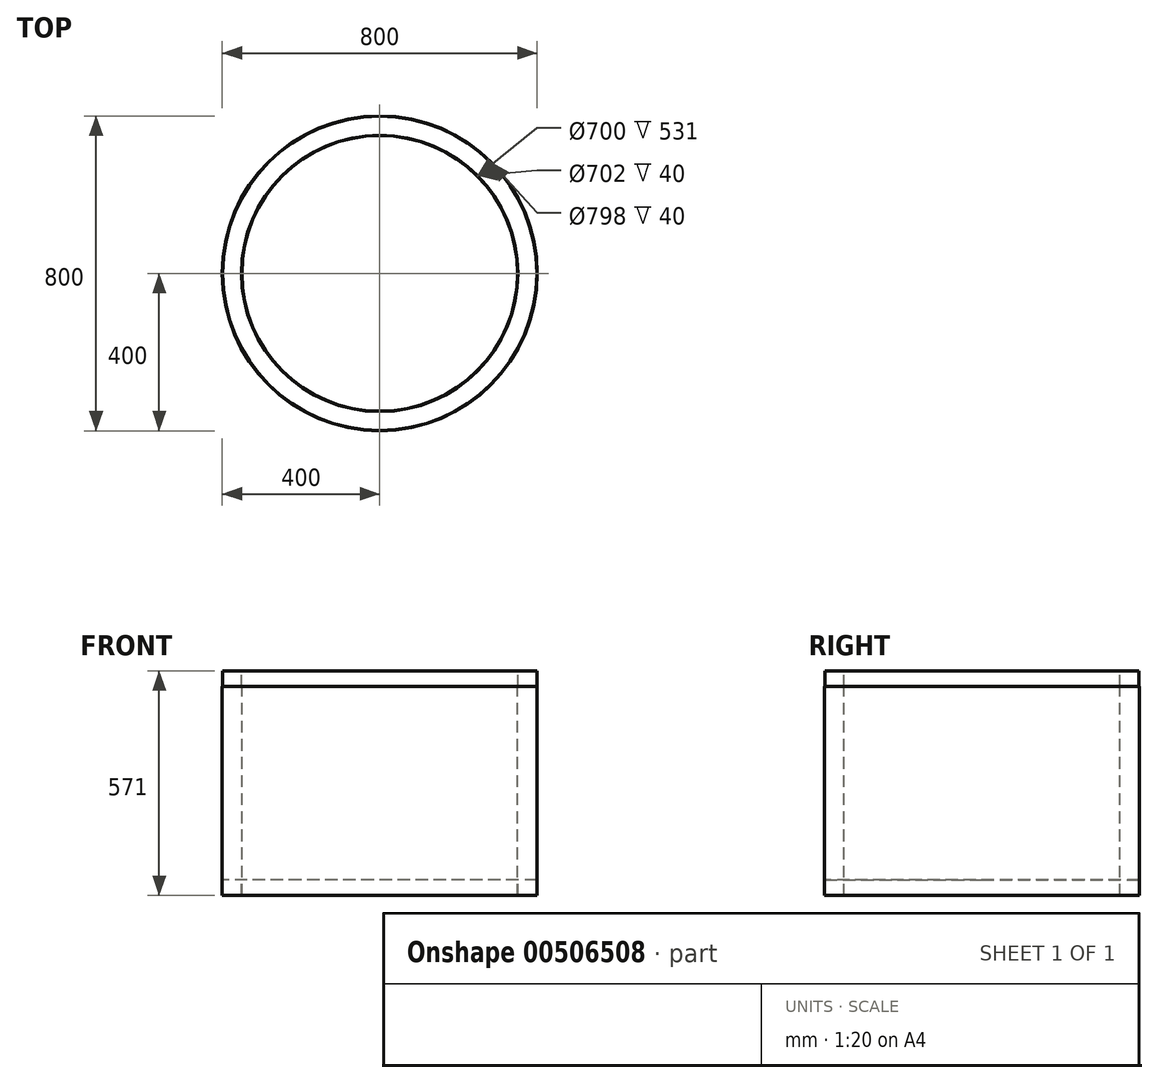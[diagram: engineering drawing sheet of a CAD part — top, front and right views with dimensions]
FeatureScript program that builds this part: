
annotation { "Feature Type Name" : "Feature", "Feature Type Description" : "" }
export const myFeature = defineFeature(function(context is Context, id is Id, definition is map)
    precondition{}
    {
        {
            var Q0;
            Q0=qCreatedBy(makeId("Front.planeOp"),FACE);
            var sketch = newSketch(context, id + "F0", { "sketchPlane" : qUnion([Q0])});
            skLineSegment(sketch, "E0", {"start": v(0, 74.87) * mm, "end": v(0, -73.71) * mm, "construction": true});
            skLineSegment(sketch, "E1", {"start": v(0, 374.84) * mm, "end": v(0, -528.94) * mm, "construction": true});
            skLineSegment(sketch, "E2", {"start": v(-350, -489.75) * mm, "end": v(-350, 41.25) * mm});
            skLineSegment(sketch, "E3", {"start": v(-350, 41.25) * mm, "end": v(-351, 41.25) * mm});
            skLineSegment(sketch, "E4", {"start": v(-351, 41.25) * mm, "end": v(-351, 81.25) * mm});
            skLineSegment(sketch, "E5", {"start": v(-351, 81.25) * mm, "end": v(-399, 81.25) * mm});
            skLineSegment(sketch, "E6", {"start": v(-399, 81.25) * mm, "end": v(-399, 41.25) * mm});
            skLineSegment(sketch, "E7", {"start": v(-399, 41.25) * mm, "end": v(-400, 41.25) * mm});
            skLineSegment(sketch, "E8", {"start": v(-400, 41.25) * mm, "end": v(-400, -489.75) * mm});
            skLineSegment(sketch, "E9", {"start": v(-400, -489.75) * mm, "end": v(-399, -489.75) * mm});
            skLineSegment(sketch, "E10", {"start": v(-399, -489.75) * mm, "end": v(-399, -449.75) * mm});
            skLineSegment(sketch, "E11", {"start": v(-399, -449.75) * mm, "end": v(-351, -449.75) * mm});
            skLineSegment(sketch, "E12", {"start": v(-351, -449.75) * mm, "end": v(-351, -489.75) * mm});
            skLineSegment(sketch, "E13", {"start": v(-351, -489.75) * mm, "end": v(-350, -489.75) * mm});
            skSolve(sketch);
        }
        {
            var Q0;
            Q0=qSketchRegion(id+"F0",true);
            var Q1;
            Q1=sQuery(id+"F0.wireOp",EDGE,"E1");
            revolve(context, id + "F1", {"entities" : qUnion([Q0]), "axis" : qUnion([Q1]), "revolveType" : RevolveType.FULL});
        }
    });
